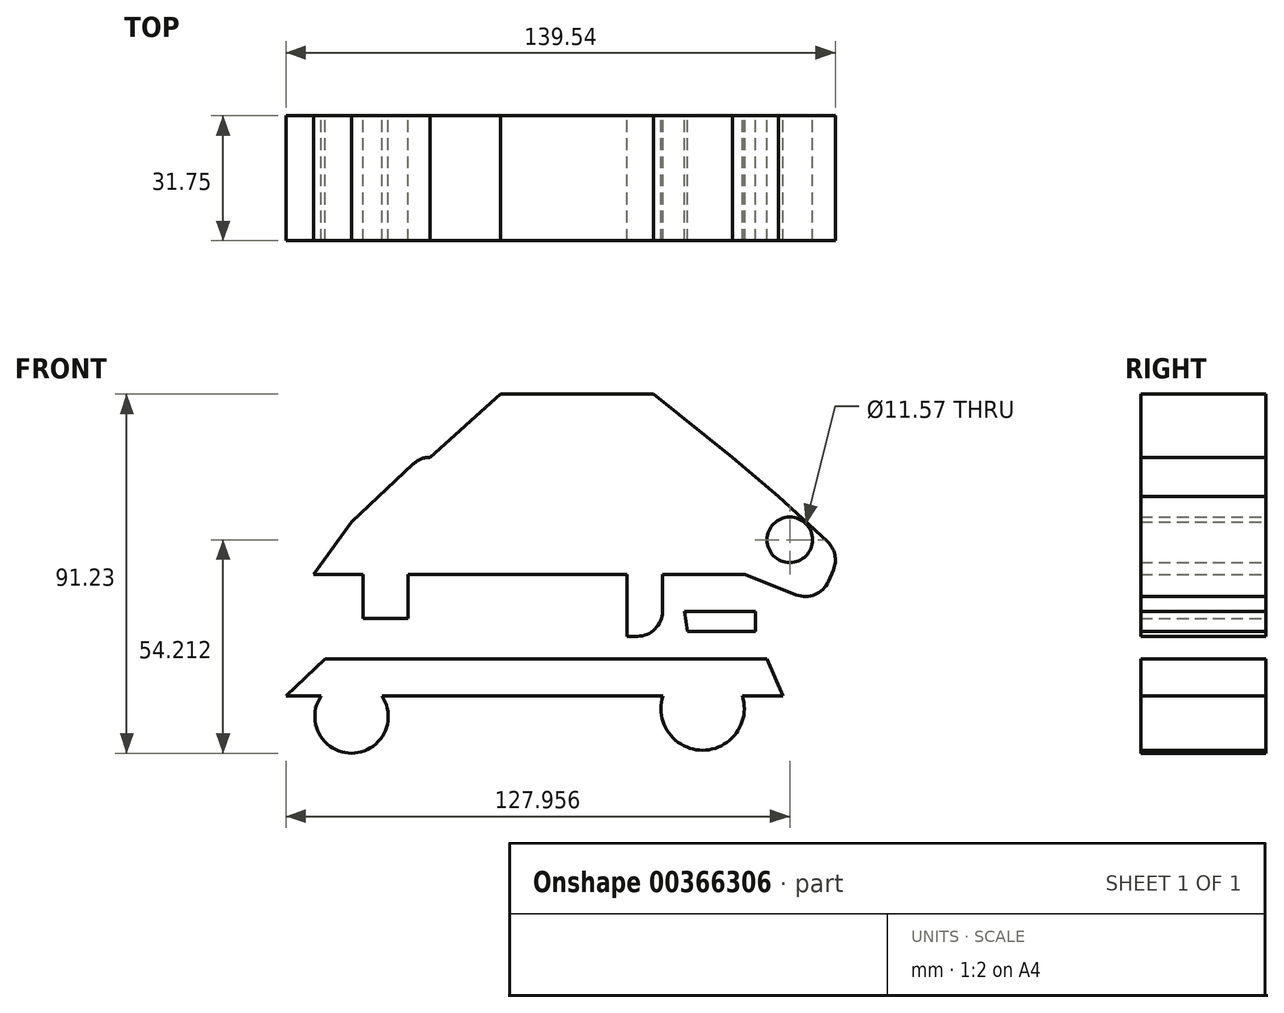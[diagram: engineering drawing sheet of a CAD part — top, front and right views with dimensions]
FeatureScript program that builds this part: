
annotation { "Feature Type Name" : "Feature", "Feature Type Description" : "" }
export const myFeature = defineFeature(function(context is Context, id is Id, definition is map)
    precondition{}
    {
        {
            var Q0;
            Q0=qCreatedBy(makeId("Front.planeOp"),FACE);
            var sketch = newSketch(context, id + "F0", { "sketchPlane" : qUnion([Q0])});
            skLineSegment(sketch, "E0", {"start": v(-36.83, 16.47) * mm, "end": v(39.93, 16.47) * mm});
            skLineSegment(sketch, "E1", {"start": v(39.93, 16.47) * mm, "end": v(51.6, 6.56) * mm});
            skLineSegment(sketch, "E2", {"start": v(-41.18, 14.74) * mm, "end": v(-56.84, 0) * mm});
            skLineSegment(sketch, "E3", {"start": v(-38.18, -13.26) * mm, "end": v(13.12, -13.26) * mm});
            skLineSegment(sketch, "E4", {"start": v(-55.09, -31.92) * mm, "end": v(-53.86, -31.92) * mm});
            skLineSegment(sketch, "E5", {"start": v(13.12, -13.26) * mm, "end": v(13.12, -29) * mm});
            skLineSegment(sketch, "E6", {"start": v(13.12, -29) * mm, "end": v(15.8, -29) * mm});
            skLineSegment(sketch, "E7", {"start": v(22.15, -22.65) * mm, "end": v(22.15, -13.26) * mm});
            skLineSegment(sketch, "E8", {"start": v(-56.84, 0) * mm, "end": v(-31.48, 0) * mm});
            skLineSegment(sketch, "E9", {"start": v(-31.48, 0) * mm, "end": v(-21.86, 16.47) * mm});
            skLineSegment(sketch, "E10", {"start": v(-31.48, 0) * mm, "end": v(-5.54, 0) * mm});
            skLineSegment(sketch, "E11", {"start": v(-5.54, 0) * mm, "end": v(0, 16.47) * mm});
            skLineSegment(sketch, "E12", {"start": v(-5.54, 0) * mm, "end": v(14.87, 0) * mm});
            skLineSegment(sketch, "E13", {"start": v(14.87, 0) * mm, "end": v(18.95, 16.47) * mm});
            skLineSegment(sketch, "E14", {"start": v(14.87, 0) * mm, "end": v(37.6, 0) * mm});
            skLineSegment(sketch, "E15", {"start": v(37.6, 0) * mm, "end": v(39.93, 16.47) * mm});
            skLineSegment(sketch, "E16", {"start": v(-31.48, 0) * mm, "end": v(-38.18, -13.26) * mm});
            skLineSegment(sketch, "E17", {"start": v(-5.54, 0) * mm, "end": v(-11.66, -13.26) * mm});
            skLineSegment(sketch, "E18", {"start": v(14.87, 0) * mm, "end": v(13.12, -13.26) * mm});
            skLineSegment(sketch, "E19", {"start": v(37.6, 0) * mm, "end": v(37.6, -13.26) * mm});
            skLineSegment(sketch, "E20", {"start": v(43.14, -13.26) * mm, "end": v(51.6, 6.56) * mm});
            skLineSegment(sketch, "E21", {"start": v(51.6, 6.56) * mm, "end": v(64.05, -4.98) * mm});
            skLineSegment(sketch, "E22", {"start": v(65.58, -12.13) * mm, "end": v(64.32, -15.07) * mm});
            skLineSegment(sketch, "E23", {"start": v(56.11, -18.47) * mm, "end": v(43.14, -13.26) * mm});
            skCircle(sketch, "E24", {"center": v(54.5, -4.52) * mm, "radius": 5.79 * mm});
            skPoint(sketch, "E25.visualSharp", {"position": v(-39.35, 16.47) * mm});
            skArc(sketch, "E25.filletArc", {"start": v(-36.83, 16.47) * mm, "mid": v(-39.17, 16.02) * mm, "end": v(-41.18, 14.74) * mm});
            skPoint(sketch, "E26.visualSharp", {"position": v(-66.46, -13.26) * mm});
            skPoint(sketch, "E27.visualSharp", {"position": v(61.88, -20.8) * mm});
            skArc(sketch, "E27.filletArc", {"start": v(56.11, -18.47) * mm, "mid": v(60.91, -18.45) * mm, "end": v(64.32, -15.07) * mm});
            skPoint(sketch, "E28.visualSharp", {"position": v(67.33, -8.02) * mm});
            skArc(sketch, "E28.filletArc", {"start": v(65.58, -12.13) * mm, "mid": v(65.95, -8.31) * mm, "end": v(64.05, -4.98) * mm});
            skPoint(sketch, "E29.visualSharp", {"position": v(22.15, -29) * mm});
            skArc(sketch, "E29.filletArc", {"start": v(15.8, -29) * mm, "mid": v(20.3, -27.14) * mm, "end": v(22.15, -22.65) * mm});
            skPoint(sketch, "E30.visualSharp", {"position": v(-47.51, -31.92) * mm});
            skLineSegment(sketch, "E31", {"start": v(-36.83, 16.47) * mm, "end": v(-18.95, 32.5) * mm});
            skLineSegment(sketch, "E32", {"start": v(-18.95, 32.5) * mm, "end": v(-21.86, 16.47) * mm});
            skLineSegment(sketch, "E33", {"start": v(-18.95, 32.5) * mm, "end": v(0, 32.5) * mm});
            skLineSegment(sketch, "E34", {"start": v(0, 32.5) * mm, "end": v(0, 16.47) * mm});
            skLineSegment(sketch, "E35", {"start": v(0, 32.5) * mm, "end": v(19.82, 32.5) * mm});
            skLineSegment(sketch, "E36", {"start": v(19.82, 32.5) * mm, "end": v(18.95, 16.47) * mm});
            skLineSegment(sketch, "E37", {"start": v(19.82, 32.5) * mm, "end": v(39.93, 16.47) * mm});
            skLineSegment(sketch, "E38", {"start": v(37.6, 0) * mm, "end": v(47.36, -4.16) * mm});
            skPoint(sketch, "E38.endSnap0", {"position": v(47.36, -3.35) * mm});
            skLineSegment(sketch, "E39", {"start": v(-63.54, -34.83) * mm, "end": v(48.68, -34.83) * mm});
            skLineSegment(sketch, "E40", {"start": v(48.68, -34.83) * mm, "end": v(52.76, -44.16) * mm});
            skLineSegment(sketch, "E41", {"start": v(52.76, -44.16) * mm, "end": v(-73.45, -44.16) * mm});
            skLineSegment(sketch, "E42", {"start": v(-73.45, -44.16) * mm, "end": v(-63.54, -34.83) * mm});
            skCircle(sketch, "E43", {"center": v(-56.84, -49.4) * mm, "radius": 9.33 * mm});
            skCircle(sketch, "E44", {"center": v(32.35, -47.36) * mm, "radius": 10.6 * mm});
            skLineSegment(sketch, "E45.trimOffspring", {"start": v(22.15, -13.26) * mm, "end": v(43.14, -13.26) * mm});
            skLineSegment(sketch, "E46", {"start": v(-56.84, 0) * mm, "end": v(-66.46, -13.26) * mm});
            skLineSegment(sketch, "E47", {"start": v(-66.46, -13.26) * mm, "end": v(-53.88, -13.26) * mm});
            skLineSegment(sketch, "E48", {"start": v(-53.88, -13.26) * mm, "end": v(-53.88, -24.47) * mm});
            skLineSegment(sketch, "E49", {"start": v(-53.88, -24.47) * mm, "end": v(-42.51, -24.47) * mm});
            skLineSegment(sketch, "E50", {"start": v(-42.51, -24.47) * mm, "end": v(-42.51, -13.26) * mm});
            skLineSegment(sketch, "E51", {"start": v(-42.51, -13.26) * mm, "end": v(-38.18, -13.26) * mm});
            skLineSegment(sketch, "E52", {"start": v(27.7, -22.65) * mm, "end": v(45.76, -22.65) * mm});
            skLineSegment(sketch, "E53", {"start": v(45.76, -22.65) * mm, "end": v(45.76, -27.84) * mm});
            skLineSegment(sketch, "E54", {"start": v(45.76, -27.84) * mm, "end": v(28.56, -27.84) * mm});
            skLineSegment(sketch, "E55", {"start": v(28.56, -27.84) * mm, "end": v(27.7, -22.65) * mm});
            skSolve(sketch);
        }
        {
            var Q0;
            Q0 = qSketchRegion(id + "F0", true);
            var Q1;
            {var subQ0=sQuery(id+"F0.wireOp",EDGE,"E9");Q1=makeQuery(id+"F0.imprint","IMPRINT",FACE,{"disambiguationData":[TD([[makeQuery(id+"F0.imprint","IMPRINT",EDGE,{"derivedFrom":subQ0}),-1.0]])]});}
            var Q2;
            {var subQ0=sQuery(id+"F0.wireOp",EDGE,"E11");Q2=makeQuery(id+"F0.imprint","IMPRINT",FACE,{"disambiguationData":[TD([[makeQuery(id+"F0.imprint","IMPRINT",EDGE,{"derivedFrom":subQ0}),-1.0]])]});}
            extrude(context, id + "F1", {"entities" : qUnion([Q0, Q1, Q2]), "depth" : 31.75 * mm});
        }
    });
